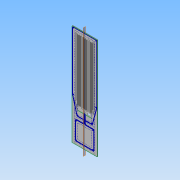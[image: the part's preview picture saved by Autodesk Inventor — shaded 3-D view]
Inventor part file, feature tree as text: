
AUTODESK INVENTOR PART (.ipt)
format: ipt  version: 2013 (Build 170138000, 138)  size: 451,072 bytes
history: native  units: in
note: dims shown in document units (in); Inventor stores cm internally (conversion verified against a paired STEP export)
features: other x15, extrude x5, hole x1, plane x1
ambient origin geometry x8: Origin, YZ Plane, XZ Plane, XY Plane, X Axis, Y Axis, Z Axis, Center Point
bodies: Solid1 (feature_tree)
feature tree (22):
  other  "Blocks"
  extrude  "Stock Extrusion"  Depth=23.8125in
  extrude  "Main rope pocket"  Depth=96.0in
  other  "Side profile reference"
  hole  "Hole1"  [1 undecoded]
  plane  "Work Plane1"
  extrude  "Through Panel Extrusion5"  Depth=58.0in
  other  "Exclaim Point"
  other  "Removal extra wood"
  other  "SignCenter"
  extrude  "Point pocket"  Depth=1.0in
  extrude  "Extrusion8"  Depth=2.9062in
  other  "Stock"
  other  "LEDPocket"
  other  "TwoLineColumn"
  other  "TwoLineColumnEnd"
  other  "15mm Neon profile"
  other  "U Bolt hole and bore"
  other  "U-Bolt holes"
  other  "WeatherProof panel"
  other  "15mm Neon profile:1"
  other  "15mm Neon profile:2"
note: 1 required parameter value undecoded (feature->parameter linkage not recoverable at this tier; creation-order binding heuristic only, values carry confidence <= 0.55)
